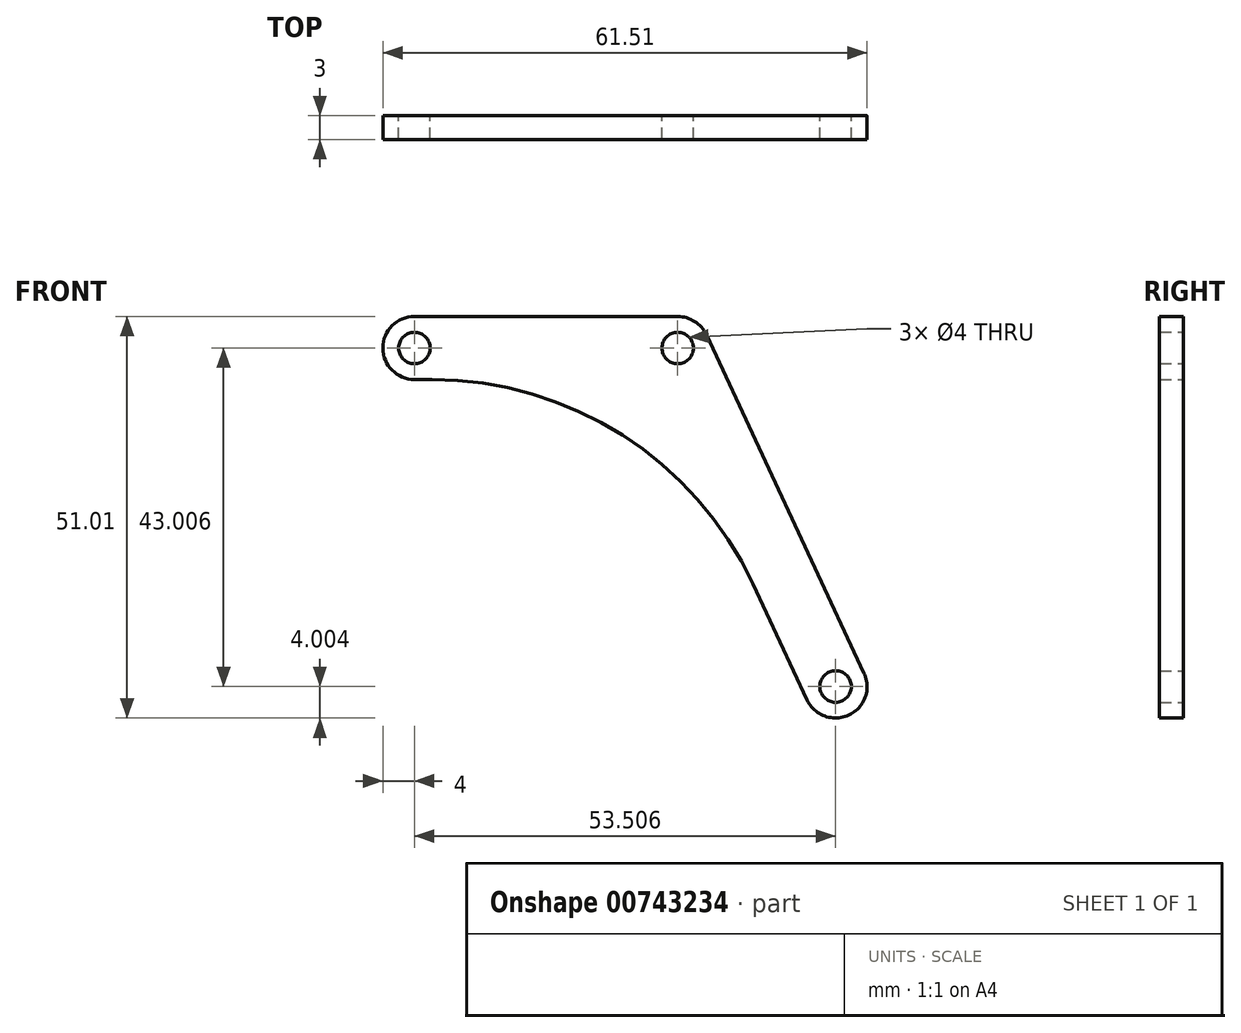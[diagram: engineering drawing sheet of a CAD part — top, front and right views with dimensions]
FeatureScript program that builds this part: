
annotation { "Feature Type Name" : "Feature", "Feature Type Description" : "" }
export const myFeature = defineFeature(function(context is Context, id is Id, definition is map)
    precondition{}
    {
        {
            var Q0;
            Q0=qCreatedBy(makeId("Front.planeOp"),FACE);
            var sketch = newSketch(context, id + "F0", { "sketchPlane" : qUnion([Q0])});
            skLineSegment(sketch, "E0", {"start": v(-2.55, 0) * mm, "end": v(-36, 0) * mm});
            skLineSegment(sketch, "E1", {"start": v(-36, 0) * mm, "end": v(-36, -8) * mm, "construction": true});
            skLineSegment(sketch, "E2", {"start": v(-36, -8) * mm, "end": v(-33.76, -8) * mm});
            skLineSegment(sketch, "E3", {"start": v(7.02, -33.98) * mm, "end": v(13.88, -48.7) * mm});
            skLineSegment(sketch, "E4", {"start": v(13.88, -48.7) * mm, "end": v(21.13, -45.32) * mm, "construction": true});
            skLineSegment(sketch, "E5", {"start": v(21.13, -45.32) * mm, "end": v(1.08, -2.3) * mm});
            skArc(sketch, "E6", {"start": v(-36, 0) * mm, "mid": v(-40, -4) * mm, "end": v(-36, -8) * mm});
            skArc(sketch, "E7", {"start": v(13.88, -48.7) * mm, "mid": v(19.2, -50.63) * mm, "end": v(21.13, -45.32) * mm});
            skPoint(sketch, "E8.visualSharp", {"position": v(-5.1, -8) * mm});
            skArc(sketch, "E8.filletArc", {"start": v(7.02, -33.98) * mm, "mid": v(-9.59, -15.05) * mm, "end": v(-33.76, -8) * mm});
            skPoint(sketch, "E9.visualSharp", {"position": v(0, 0) * mm});
            skArc(sketch, "E9.filletArc", {"start": v(1.08, -2.3) * mm, "mid": v(-0.4, -0.63) * mm, "end": v(-2.55, 0) * mm});
            skCircle(sketch, "E10", {"center": v(-36, -4) * mm, "radius": 2 * mm});
            skCircle(sketch, "E11", {"center": v(-2.55, -4) * mm, "radius": 2 * mm});
            skCircle(sketch, "E12", {"center": v(17.5, -47) * mm, "radius": 2 * mm});
            skSolve(sketch);
        }
        {
            var Q0;
            Q0=qSketchRegion(id+"F0",true);
            extrude(context, id + "F1", {"entities" : qUnion([Q0]), "depth" : 3 * mm, "offsetDistance" : 25 * mm});
        }
    });
